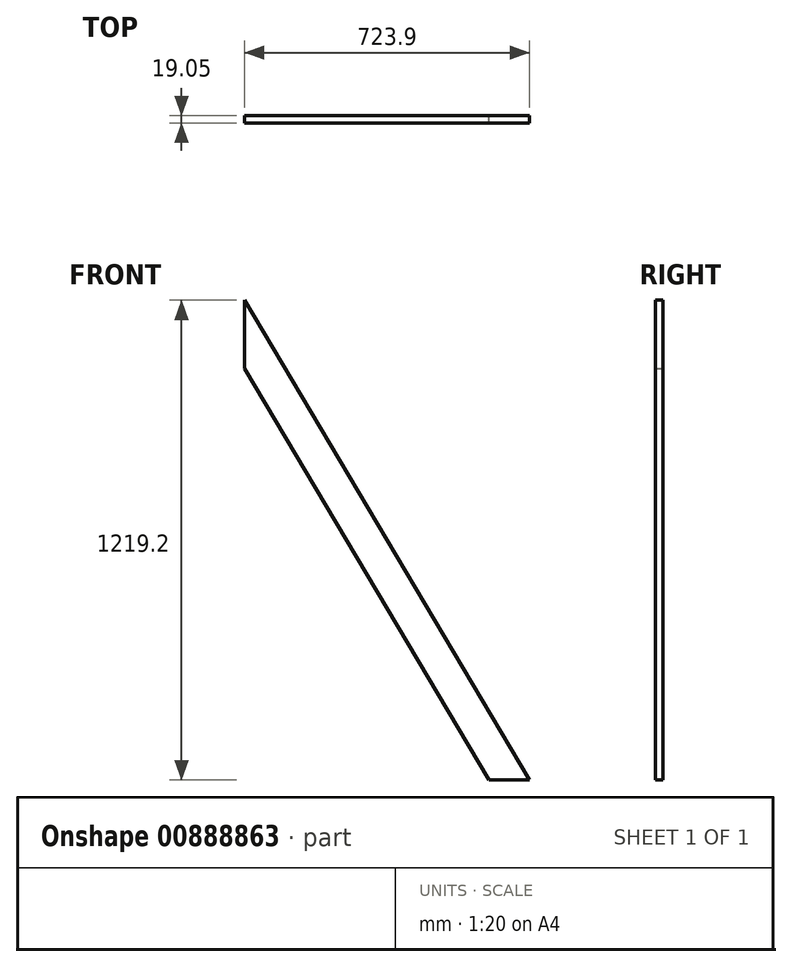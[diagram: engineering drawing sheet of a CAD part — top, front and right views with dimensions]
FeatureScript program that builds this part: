
annotation { "Feature Type Name" : "Feature", "Feature Type Description" : "" }
export const myFeature = defineFeature(function(context is Context, id is Id, definition is map)
    precondition{}
    {
        {
            var Q0;
            Q0=qCreatedBy(makeId("Front.planeOp"),FACE);
            var sketch = newSketch(context, id + "F0", { "sketchPlane" : qUnion([Q0])});
            skLineSegment(sketch, "E0", {"start": v(0, 0) * mm, "end": v(-103.39, 0) * mm});
            skLineSegment(sketch, "E1", {"start": v(-103.39, 0) * mm, "end": v(-723.9, 1045.07) * mm});
            skLineSegment(sketch, "E2", {"start": v(-723.9, 1045.07) * mm, "end": v(-723.9, 1219.2) * mm});
            skLineSegment(sketch, "E3", {"start": v(-723.9, 1219.2) * mm, "end": v(0, 0) * mm});
            skLineSegment(sketch, "E4", {"start": v(-723.9, 1219.2) * mm, "end": v(-723.9, 0) * mm, "construction": true});
            skLineSegment(sketch, "E5", {"start": v(-723.9, 0) * mm, "end": v(-812.8, 0) * mm, "construction": true});
            skLineSegment(sketch, "E6", {"start": v(-812.8, 0) * mm, "end": v(-812.8, 1219.2) * mm, "construction": true});
            skLineSegment(sketch, "E7", {"start": v(-812.8, 1219.2) * mm, "end": v(-723.9, 1219.2) * mm, "construction": true});
            skSolve(sketch);
        }
        {
            var Q0;
            Q0 = qSketchRegion(id + "F0", true);
            extrude(context, id + "F1", {"entities" : qUnion([Q0]), "depth" : 19.05 * mm, "offsetDistance" : 25.4 * mm});
        }
    });
